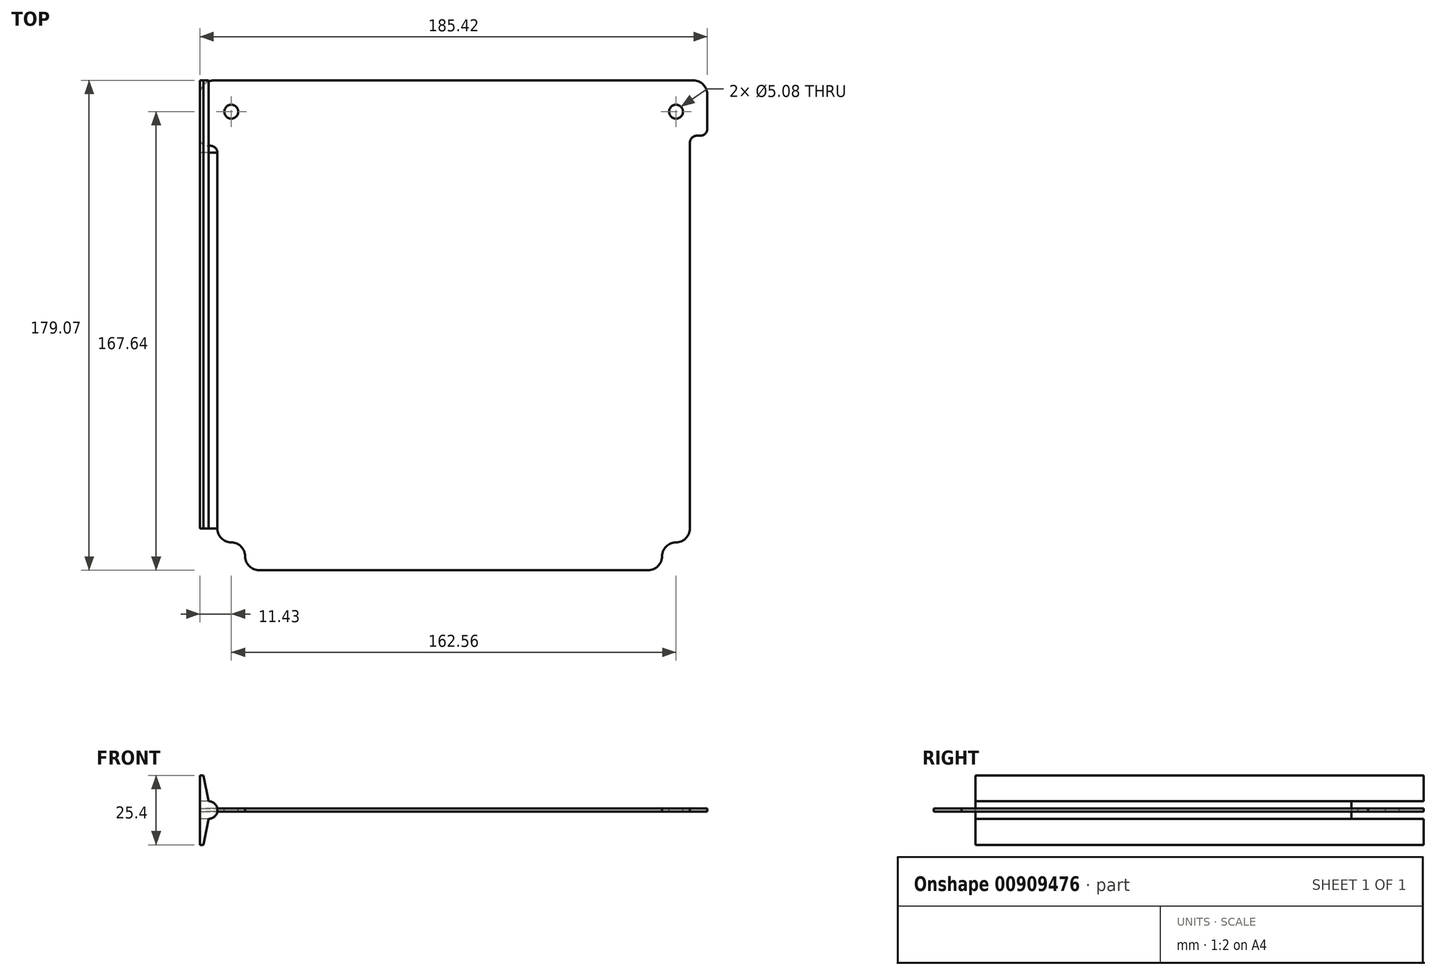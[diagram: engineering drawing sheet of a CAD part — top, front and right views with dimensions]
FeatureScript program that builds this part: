
annotation { "Feature Type Name" : "Feature", "Feature Type Description" : "" }
export const myFeature = defineFeature(function(context is Context, id is Id, definition is map)
    precondition{}
    {
        {
            var Q0;
            Q0=qCreatedBy(makeId("Top.planeOp"),FACE);
            var sketch = newSketch(context, id + "F0", { "sketchPlane" : qUnion([Q0])});
            skLineSegment(sketch, "E0.bottom", {"start": v(-92.71, -92.71) * mm, "end": v(92.71, -92.71) * mm});
            skLineSegment(sketch, "E0.top", {"start": v(-92.71, 92.71) * mm, "end": v(92.71, 92.71) * mm});
            skLineSegment(sketch, "E0.left", {"start": v(-92.71, -92.71) * mm, "end": v(-92.71, 92.71) * mm});
            skLineSegment(sketch, "E0.right", {"start": v(92.71, -92.71) * mm, "end": v(92.71, 92.71) * mm});
            skPoint(sketch, "E0.middle", {"position": v(0, 0) * mm});
            skSolve(sketch);
        }
        {
            var Q0;
            Q0 = qSketchRegion(id + "F0", true);
            extrude(context, id + "F1", {"entities" : qUnion([Q0]), "depth" : 1.22 * mm, "offsetDistance" : 25.4 * mm});
        }
        {
            var Q0;
            Q0=makeQuery(id+"F1.opExtrude","SWEPT_EDGE",EDGE,{"disambiguationData":[OSD([sQuery(id+"F0.wireOp",EDGE,"E0.top"),sQuery(id+"F0.wireOp",EDGE,"E0.left")])]});
            var Q1;
            Q1=makeQuery(id+"F1.opExtrude","SWEPT_EDGE",EDGE,{"disambiguationData":[OSD([sQuery(id+"F0.wireOp",EDGE,"E0.top"),sQuery(id+"F0.wireOp",EDGE,"E0.right")])]});
            var Q2;
            Q2=makeQuery(id+"F1.opExtrude","SWEPT_EDGE",EDGE,{"disambiguationData":[OSD([sQuery(id+"F0.wireOp",EDGE,"E0.bottom"),sQuery(id+"F0.wireOp",EDGE,"E0.right")])]});
            var Q3;
            Q3=makeQuery(id+"F1.opExtrude","SWEPT_EDGE",EDGE,{"disambiguationData":[OSD([sQuery(id+"F0.wireOp",EDGE,"E0.bottom"),sQuery(id+"F0.wireOp",EDGE,"E0.left")])]});
            fillet(context, id + "F2", {"entities" : qUnion([Q0, Q1, Q2, Q3]), "radius" : 5.08 * mm, "tangentPropagation" : true, "allowEdgeOverflow" : false});
        }
        {
            var Q0;
            Q0=makeQuery(id+"F1.opExtrude","CAP_FACE",FACE,{"disambiguationData":[OSD([sQuery(id+"F0.wireOp",EDGE,"E0.bottom"),sQuery(id+"F0.wireOp",EDGE,"E0.top"),sQuery(id+"F0.wireOp",EDGE,"E0.left"),sQuery(id+"F0.wireOp",EDGE,"E0.right")])],"isStart":false});
            var sketch = newSketch(context, id + "F3", { "sketchPlane" : qUnion([Q0])});
            skCircle(sketch, "E1", {"center": v(-81.28, 81.28) * mm, "radius": 2.54 * mm});
            skCircle(sketch, "E2", {"center": v(81.28, 81.28) * mm, "radius": 2.54 * mm});
            skCircle(sketch, "E3", {"center": v(81.28, -81.28) * mm, "radius": 2.54 * mm});
            skCircle(sketch, "E4", {"center": v(-81.28, -81.28) * mm, "radius": 2.54 * mm});
            skLineSegment(sketch, "E5.bottom", {"start": v(-81.28, 81.28) * mm, "end": v(81.28, 81.28) * mm, "construction": true});
            skLineSegment(sketch, "E5.top", {"start": v(-81.28, -81.28) * mm, "end": v(81.28, -81.28) * mm, "construction": true});
            skLineSegment(sketch, "E5.left", {"start": v(-81.28, 81.28) * mm, "end": v(-81.28, -81.28) * mm, "construction": true});
            skLineSegment(sketch, "E5.right", {"start": v(81.28, 81.28) * mm, "end": v(81.28, -81.28) * mm, "construction": true});
            skPoint(sketch, "E5.middle", {"position": v(0, 0) * mm});
            skLineSegment(sketch, "E6", {"start": v(0, 0) * mm, "end": v(-81.28, 81.28) * mm});
            skSolve(sketch);
        }
        {
            var Q0;
            Q0 = qSketchRegion(id + "F3", true);
            extrude(context, id + "F4", {"entities" : qUnion([Q0]), "operationType" : NewBodyOperationType.REMOVE, "endBound" : BoundingType.THROUGH_ALL, "oppositeDirection" : true, "depth" : 25.4 * mm, "offsetDistance" : 25.4 * mm});
        }
        {
            var Q0;
            Q0=makeQuery(id+"F1.opExtrude","CAP_FACE",FACE,{"disambiguationData":[OSD([sQuery(id+"F0.wireOp",EDGE,"E0.bottom"),sQuery(id+"F0.wireOp",EDGE,"E0.top"),sQuery(id+"F0.wireOp",EDGE,"E0.left"),sQuery(id+"F0.wireOp",EDGE,"E0.right")])],"isStart":false});
            var sketch = newSketch(context, id + "F5", { "sketchPlane" : qUnion([Q0])});
            skLineSegment(sketch, "E7.bottom", {"start": v(-125.24, 68.83) * mm, "end": v(-86.36, 68.83) * mm});
            skLineSegment(sketch, "E7.top", {"start": v(-125.24, -120.32) * mm, "end": v(-86.36, -120.32) * mm});
            skLineSegment(sketch, "E7.left", {"start": v(-125.24, 68.83) * mm, "end": v(-125.24, -120.32) * mm});
            skLineSegment(sketch, "E7.right", {"start": v(-86.36, 68.83) * mm, "end": v(-86.36, -71.12) * mm});
            skLineSegment(sketch, "E8.bottom", {"start": v(127.16, 72.5) * mm, "end": v(86.36, 72.5) * mm});
            skLineSegment(sketch, "E8.top", {"start": v(127.16, -120.32) * mm, "end": v(-86.36, -120.32) * mm});
            skLineSegment(sketch, "E8.left", {"start": v(127.16, 72.5) * mm, "end": v(127.16, -120.32) * mm});
            skLineSegment(sketch, "E8.right", {"start": v(86.36, 72.5) * mm, "end": v(86.36, -71.12) * mm});
            skLineSegment(sketch, "E9", {"start": v(-86.36, 0) * mm, "end": v(0, 0) * mm, "construction": true});
            skLineSegment(sketch, "E10", {"start": v(0, 0) * mm, "end": v(86.36, 0) * mm, "construction": true});
            skPoint(sketch, "E10.endSnap0", {"position": v(92.71, 0) * mm});
            skArc(sketch, "E11", {"start": v(-86.36, -71.12) * mm, "mid": v(-84.87, -74.71) * mm, "end": v(-81.28, -76.2) * mm});
            skArc(sketch, "E12", {"start": v(-76.2, -81.28) * mm, "mid": v(-77.69, -77.69) * mm, "end": v(-81.28, -76.2) * mm});
            skLineSegment(sketch, "E13", {"start": v(-71.12, -86.36) * mm, "end": v(71.12, -86.36) * mm});
            skArc(sketch, "E14", {"start": v(-76.2, -81.28) * mm, "mid": v(-74.71, -84.87) * mm, "end": v(-71.12, -86.36) * mm});
            skArc(sketch, "E15", {"start": v(81.28, -76.2) * mm, "mid": v(84.87, -74.71) * mm, "end": v(86.36, -71.12) * mm});
            skArc(sketch, "E16", {"start": v(81.28, -76.2) * mm, "mid": v(77.69, -77.69) * mm, "end": v(76.2, -81.28) * mm});
            skArc(sketch, "E17", {"start": v(71.12, -86.36) * mm, "mid": v(74.71, -84.87) * mm, "end": v(76.2, -81.28) * mm});
            skSolve(sketch);
        }
        {
            var Q0;
            Q0 = qSketchRegion(id + "F5", true);
            extrude(context, id + "F6", {"entities" : qUnion([Q0]), "operationType" : NewBodyOperationType.REMOVE, "endBound" : BoundingType.THROUGH_ALL, "oppositeDirection" : true, "depth" : 25.4 * mm, "offsetDistance" : 25.4 * mm});
        }
        {
            var Q0;
            Q0=makeQuery(id+"F6.boolean.opBoolean","COPY",EDGE,{"derivedFrom":makeQuery(id+"F6.opExtrude","SWEPT_EDGE",EDGE,{"disambiguationData":[OSD([sQuery(id+"F5.wireOp",EDGE,"E7.bottom"),sQuery(id+"F5.wireOp",EDGE,"E7.right")])]})});
            var Q1;
            Q1=makeQuery(id+"F6.boolean.opBoolean","INTERSECT",EDGE,{"derivedFrom":[makeQuery(id+"F1.opExtrude","SWEPT_FACE",FACE,{"disambiguationData":[OSD([sQuery(id+"F0.wireOp",EDGE,"E0.left")])]}),makeQuery(id+"F6.opExtrude","SWEPT_FACE",FACE,{"disambiguationData":[OSD([sQuery(id+"F5.wireOp",EDGE,"E7.bottom")])]})]});
            var Q2;
            Q2=makeQuery(id+"F6.boolean.opBoolean","INTERSECT",EDGE,{"derivedFrom":[makeQuery(id+"F1.opExtrude","SWEPT_FACE",FACE,{"disambiguationData":[OSD([sQuery(id+"F0.wireOp",EDGE,"E0.right")])]}),makeQuery(id+"F6.opExtrude","SWEPT_FACE",FACE,{"disambiguationData":[OSD([sQuery(id+"F5.wireOp",EDGE,"E8.bottom")])]})]});
            var Q3;
            Q3=makeQuery(id+"F6.boolean.opBoolean","COPY",EDGE,{"derivedFrom":makeQuery(id+"F6.opExtrude","SWEPT_EDGE",EDGE,{"disambiguationData":[OSD([sQuery(id+"F5.wireOp",EDGE,"E8.bottom"),sQuery(id+"F5.wireOp",EDGE,"E8.right")])]})});
            fillet(context, id + "F7", {"entities" : qUnion([Q0, Q1, Q2, Q3]), "radius" : 2.54 * mm, "tangentPropagation" : true, "allowEdgeOverflow" : false});
        }
        {
            var Q0;
            Q0=qCreatedBy(makeId("Front.planeOp"),FACE);
            var Q1;
            Q1=makeQuery(id+"F6.boolean.opBoolean","COPY",EDGE,{"derivedFrom":makeQuery(id+"F6.opExtrude","SWEPT_EDGE",EDGE,{"disambiguationData":[OSD([sQuery(id+"F5.wireOp",EDGE,"E7.right"),sQuery(id+"F5.wireOp",EDGE,"E11")])]})});
            cPlane(context, id + "F8", {"entities" : qUnion([Q0, Q1]), "cplaneType" : CPlaneType.LINE_ANGLE, "offset" : 25.4 * mm, "angle" : 0 * degree, "width" : 152.4 * mm, "height" : 152.4 * mm});
        }
        {
            var Q0;
            Q0=qCreatedBy(id+"F8.planeOp",FACE);
            var sketch = newSketch(context, id + "F9", { "sketchPlane" : qUnion([Q0])});
            skCircle(sketch, "E18", {"center": v(89.5, 0.6) * mm, "radius": 3.2 * mm});
            skSolve(sketch);
        }
        {
            var Q0;
            Q0 = qSketchRegion(id + "F9", true);
            extrude(context, id + "F10", {"entities" : qUnion([Q0]), "operationType" : NewBodyOperationType.ADD, "depth" : 137.4 * mm, "offsetDistance" : 25.4 * mm});
        }
        {
            var Q0;
            Q0=makeQuery(id+"F10.opExtrude","CAP_FACE",FACE,{"disambiguationData":[OSD([sQuery(id+"F9.wireOp",EDGE,"E18")])],"isStart":true});
            var sketch = newSketch(context, id + "F11", { "sketchPlane" : qUnion([Q0])});
            skLineSegment(sketch, "E19", {"start": v(-92.71, 13.3) * mm, "end": v(-92.71, -12.1) * mm});
            skLineSegment(sketch, "E20", {"start": v(-89.5, -2.6) * mm, "end": v(-89.5, 3.81) * mm});
            skLineSegment(sketch, "E21", {"start": v(-89.5, 0.6) * mm, "end": v(-92.7, 0.6) * mm, "construction": true});
            skLineSegment(sketch, "E22", {"start": v(-92.71, -12.1) * mm, "end": v(-91.5, -12.1) * mm});
            skLineSegment(sketch, "E23", {"start": v(-92.71, 13.3) * mm, "end": v(-91.5, 13.3) * mm});
            skLineSegment(sketch, "E24", {"start": v(-89.5, 3.81) * mm, "end": v(-91.5, 13.3) * mm});
            skLineSegment(sketch, "E25", {"start": v(-89.5, -2.6) * mm, "end": v(-91.5, -12.1) * mm});
            skSolve(sketch);
        }
        {
            var Q0;
            Q0 = qSketchRegion(id + "F11", true);
            extrude(context, id + "F12", {"entities" : qUnion([Q0]), "operationType" : NewBodyOperationType.ADD, "oppositeDirection" : true, "depth" : 137.4 * mm, "offsetDistance" : 25.4 * mm});
        }
        {
            var Q0;
            Q0=makeQuery(id+"F12.boolean.opBoolean","MERGE",FACE,{"derivedFrom":[makeQuery(id+"F10.opExtrude","CAP_FACE",FACE,{"disambiguationData":[OSD([sQuery(id+"F9.wireOp",EDGE,"E18")])],"isStart":false}),makeQuery(id+"F12.opExtrude","CAP_FACE",FACE,{"disambiguationData":[OSD([sQuery(id+"F11.wireOp",EDGE,"E19"),sQuery(id+"F11.wireOp",EDGE,"E20"),sQuery(id+"F11.wireOp",EDGE,"E22"),sQuery(id+"F11.wireOp",EDGE,"E23"),sQuery(id+"F11.wireOp",EDGE,"E24"),sQuery(id+"F11.wireOp",EDGE,"E25")])],"isStart":false})]});
            var sketch = newSketch(context, id + "F13", { "sketchPlane" : qUnion([Q0])});
            skLineSegment(sketch, "E26", {"start": v(89.5, 3.81) * mm, "end": v(92.71, 3.81) * mm});
            skLineSegment(sketch, "E27", {"start": v(92.71, 3.81) * mm, "end": v(92.71, 13.3) * mm});
            skLineSegment(sketch, "E28", {"start": v(92.71, 13.3) * mm, "end": v(91.5, 13.3) * mm});
            skLineSegment(sketch, "E29", {"start": v(91.5, 13.3) * mm, "end": v(89.5, 3.81) * mm});
            skLineSegment(sketch, "E30", {"start": v(89.5, -2.6) * mm, "end": v(92.71, -2.6) * mm});
            skLineSegment(sketch, "E31", {"start": v(92.71, -2.6) * mm, "end": v(92.71, -12.1) * mm});
            skLineSegment(sketch, "E32", {"start": v(92.71, -12.1) * mm, "end": v(91.5, -12.1) * mm});
            skLineSegment(sketch, "E33", {"start": v(91.5, -12.1) * mm, "end": v(89.5, -2.6) * mm});
            skSolve(sketch);
        }
        {
            var Q0;
            Q0 = qSketchRegion(id + "F13", true);
            var Q1;
            Q1=makeQuery(id+"F1.opExtrude","SWEPT_FACE",FACE,{"disambiguationData":[OSD([sQuery(id+"F0.wireOp",EDGE,"E0.top")])]});
            extrude(context, id + "F14", {"entities" : qUnion([Q0]), "operationType" : NewBodyOperationType.ADD, "endBound" : BoundingType.UP_TO_SURFACE, "depth" : 25.4 * mm, "endBoundEntityFace" : qUnion([Q1]), "offsetDistance" : 25.4 * mm});
        }
    });
